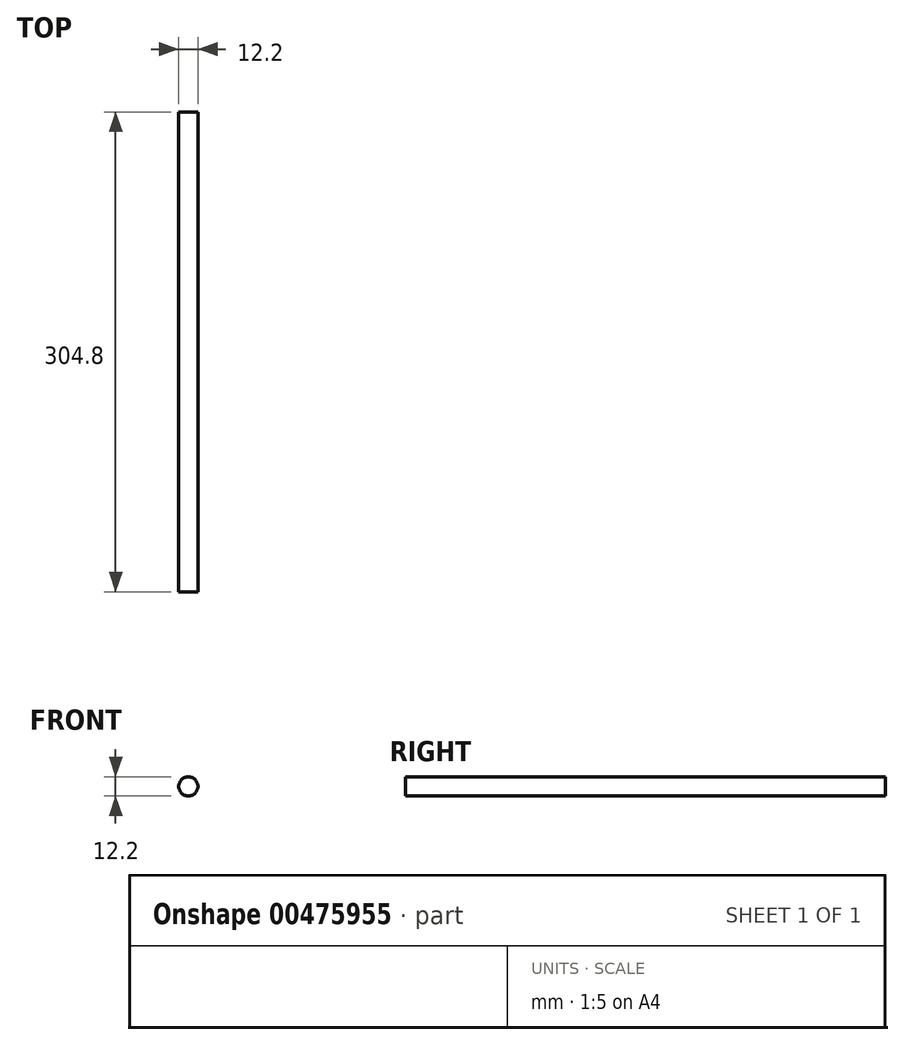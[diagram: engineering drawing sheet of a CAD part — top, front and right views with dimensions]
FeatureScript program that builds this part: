
annotation { "Feature Type Name" : "Feature", "Feature Type Description" : "" }
export const myFeature = defineFeature(function(context is Context, id is Id, definition is map)
    precondition{}
    {
        {
            var Q0;
            Q0=qCreatedBy(makeId("Front.planeOp"),FACE);
            var sketch = newSketch(context, id + "F0", { "sketchPlane" : qUnion([Q0])});
            skCircle(sketch, "E0", {"center": v(0, 0) * mm, "radius": 6.1 * mm});
            skCircle(sketch, "E1", {"center": v(0, 0) * mm, "radius": 6.31 * mm});
            skSolve(sketch);
        }
        {
            var Q0;
            Q0=makeQuery(id+"F0.imprint","IMPRINT",FACE,{"disambiguationData":[TD([[makeQuery(id+"F0.imprint","IMPRINT",EDGE,{"derivedFrom":sQuery(id+"F0.wireOp",EDGE,"E0")}),1.0]])]});
            extrude(context, id + "F1", {"entities" : qUnion([Q0]), "depth" : 304.8 * mm});
        }
    });
